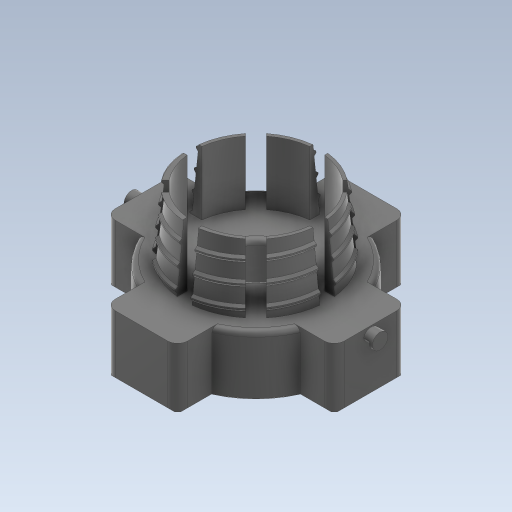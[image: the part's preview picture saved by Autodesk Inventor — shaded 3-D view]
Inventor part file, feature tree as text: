
AUTODESK INVENTOR PART (.ipt)
format: ipt  version: 2023 (Build 270158000, 158)  size: 1,051,136 bytes
history: native  units: mm
features: sketch x7, extrude x6, fillet x3, other x2, helix x2, draft x1, direct_edit x1, hole x1, pattern_circular x1, chamfer x1, projected_geometry x1
ambient origin geometry x8: Origin, YZ Plane, XZ Plane, XY Plane, X Axis, Y Axis, Z Axis, Center Point
bodies: Solid1 (feature_tree)
feature tree (26):
  other  "Slider V8 (4mm pitch)"
  extrude  "Extrusion1"  Depth=26.5mm
  draft  "FaceDraft1"
  sketch  "Sketch2"  dims[d34=0.0mm d35=0.0mm]
  helix  "Coil3"  [1 undecoded]
  helix  "Coil4"  [1 undecoded]
  direct_edit  "Direct Edit2"
  extrude  "Extrusion2"  Depth=12.0mm TaperAngle=0.0deg
  sketch  "Sketch4"  dims[d56=8.726646mm d62=4.0mm d63=13.0mm d64=10.0mm d65=1.047198mm]
  extrude  "Extrusion3"  Depth=10.0mm
  extrude  "Extrusion8"  TaperAngle=90.0deg  [1 undecoded]
  hole  "Hole1"  [1 undecoded]
  sketch  "Sketch9"  dims[d83=3.0mm d84=1.5mm d85=1.5mm d86=0.0mm d87=0.0mm d91=3.0mm d92=3.0mm d93=1.5mm d94=1.5mm d95=5.3mm d96=6.0mm d97=10.0mm d98=10.0mm d99=90.0deg d100=8.0mm d101=20.594885mm d108=35.6mm d110=3.15mm d113=1.575mm d114=7.45mm d115=2.35mm d117=3.6mm d118=0.0mm d119=1.2mm d120=0.0mm d121=20.0mm d122=360.0deg d126=1.0mm d129=0.3mm d130=2.0mm d131=45.0deg d133=14.65mm d134=14.65mm d137=23.15mm d138=46.3mm d139=46.3mm d142=1.0mm d143=2.0mm d109=0.5mm d111=0.5mm d112=0.872665mm]
  extrude  "Extrusion11"  Depth=2.0mm
  extrude  "Extrusion12"  Depth=2.0mm
  pattern_circular  "Circular Pattern1"  [2 undecoded]
  fillet  "Fillet4"  Radius=3.0mm
  chamfer  "Chamfer2"  Distance=3.0mm
  fillet  "Fillet7"  Radius=1.5mm
  fillet  "Fillet8"  Radius=1.5mm
  sketch  "Sketch1"  dims[d0=25.0mm d1=26.5mm d2=12.875mm d3=0.0mm d4=1.047198mm]
  sketch  "Sketch3"  dims[d36=7.325mm d37=7.0mm d38=7.325mm d39=0.0mm d40=7.0mm d41=28.73603mm d42=12.0mm d43=0.0mm]
  sketch  "Sketch5"  dims[d66=90.0deg d67=90.0deg d68=0.0mm d69=0.0mm d70=4.0mm d71=3.0mm d72=10.0mm d73=-1.047198mm d74=90.0deg d75=90.0deg d76=0.0mm d77=0.0mm]
  sketch  "Sketch7"  dims[d79=-0.127mm d82=3.0mm]
  projected_geometry  "Projected Loop1"
  other  "Size2"
note: 6 required parameter values undecoded (feature->parameter linkage not recoverable at this tier; creation-order binding heuristic only, values carry confidence <= 0.55)
